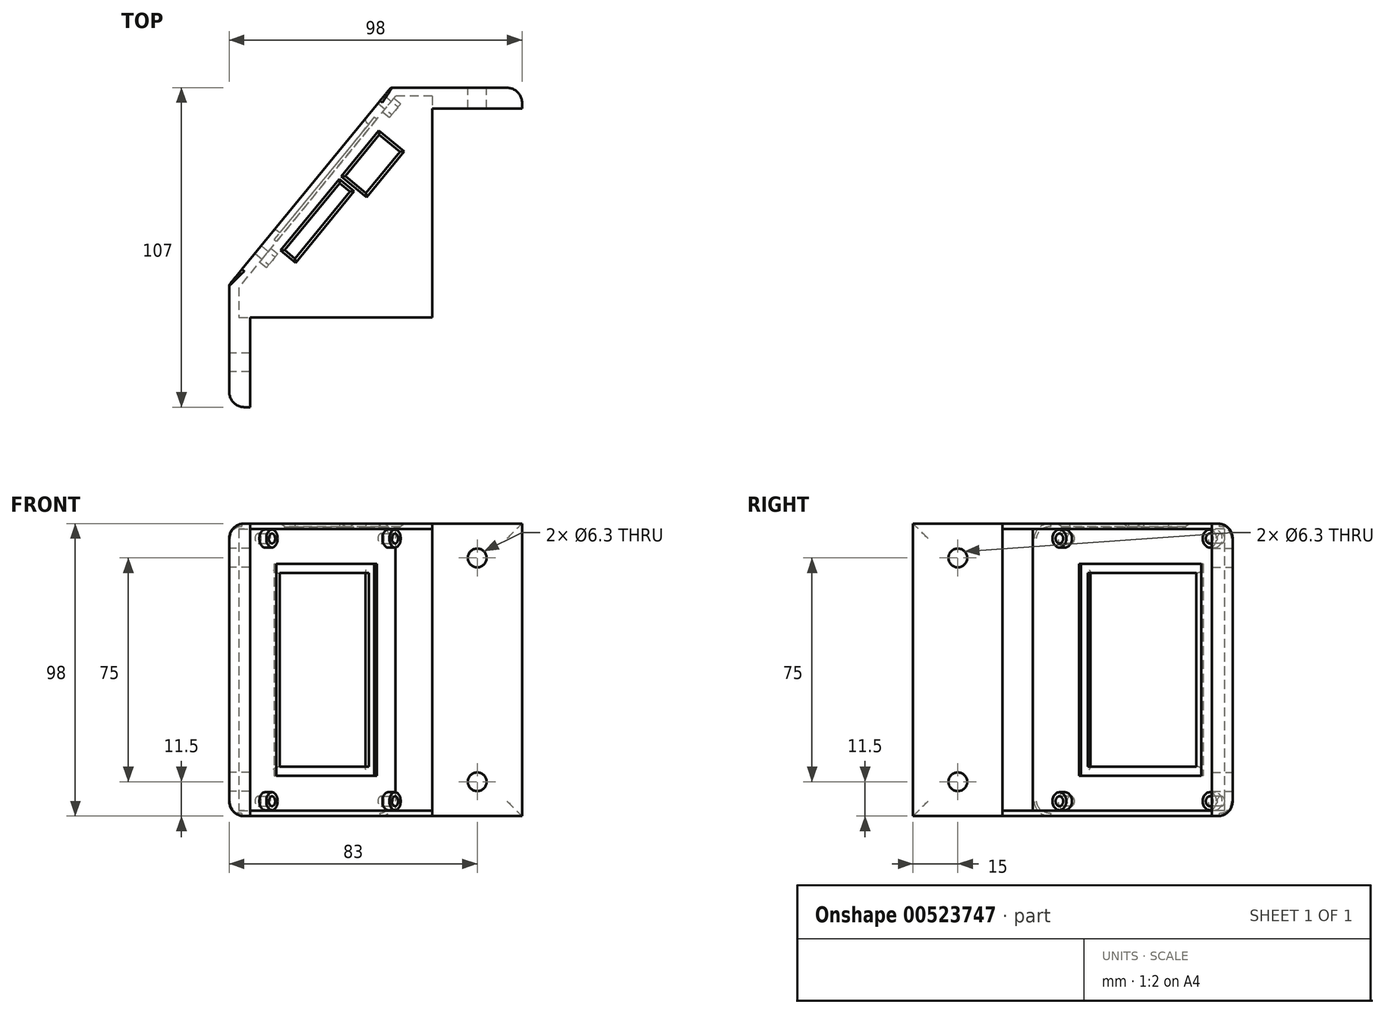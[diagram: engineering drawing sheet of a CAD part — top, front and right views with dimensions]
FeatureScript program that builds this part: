
annotation { "Feature Type Name" : "Feature", "Feature Type Description" : "" }
export const myFeature = defineFeature(function(context is Context, id is Id, definition is map)
    precondition{}
    {
        {
            var Q0;
            Q0=qCreatedBy(makeId("Top.planeOp"),FACE);
            var sketch = newSketch(context, id + "F0", { "sketchPlane" : qUnion([Q0])});
            skLineSegment(sketch, "E0.bottom", {"start": v(0, 0) * mm, "end": v(30, 0) * mm, "construction": true});
            skLineSegment(sketch, "E0.top", {"start": v(0, 30) * mm, "end": v(30, 30) * mm, "construction": true});
            skLineSegment(sketch, "E0.left", {"start": v(0, 0) * mm, "end": v(0, 30) * mm, "construction": true});
            skLineSegment(sketch, "E0.right", {"start": v(30, 0) * mm, "end": v(30, 30) * mm, "construction": true});
            skLineSegment(sketch, "E1.bottom", {"start": v(61, 70) * mm, "end": v(91, 70) * mm, "construction": true});
            skLineSegment(sketch, "E1.top", {"start": v(61, 100) * mm, "end": v(91, 100) * mm, "construction": true});
            skLineSegment(sketch, "E1.left", {"start": v(61, 70) * mm, "end": v(61, 100) * mm, "construction": true});
            skLineSegment(sketch, "E1.right", {"start": v(91, 70) * mm, "end": v(91, 100) * mm, "construction": true});
            skLineSegment(sketch, "E2", {"start": v(61, 70) * mm, "end": v(61, 100) * mm});
            skLineSegment(sketch, "E3", {"start": v(60.77, 119.05) * mm, "end": v(-24.85, 14.49) * mm});
            skLineSegment(sketch, "E4", {"start": v(61, 94.07) * mm, "end": v(8.54, 30) * mm, "construction": true});
            skLineSegment(sketch, "E5", {"start": v(61, 94.07) * mm, "end": v(48.62, 104.2) * mm, "construction": true});
            skLineSegment(sketch, "E6", {"start": v(8.54, 30) * mm, "end": v(-3.84, 40.14) * mm, "construction": true});
            skLineSegment(sketch, "E7", {"start": v(-4.85, 0) * mm, "end": v(0, 0) * mm});
            skLineSegment(sketch, "E8", {"start": v(51.37, 112.3) * mm, "end": v(-39.42, 1.43) * mm});
            skLineSegment(sketch, "E9", {"start": v(91, 100) * mm, "end": v(91, 107) * mm});
            skLineSegment(sketch, "E10", {"start": v(91, 107) * mm, "end": v(47.03, 107) * mm});
            skLineSegment(sketch, "E11", {"start": v(0, 0) * mm, "end": v(-7, 0) * mm});
            skLineSegment(sketch, "E12", {"start": v(-7, 0) * mm, "end": v(-7, 41.02) * mm});
            skLineSegment(sketch, "E13", {"start": v(91, 100) * mm, "end": v(61, 100) * mm});
            skLineSegment(sketch, "E14", {"start": v(61, 104.2) * mm, "end": v(61, 100) * mm});
            skLineSegment(sketch, "E15", {"start": v(61, 104.2) * mm, "end": v(48.62, 104.2) * mm});
            skLineSegment(sketch, "E16", {"start": v(-3.84, 40.14) * mm, "end": v(-3.84, 30) * mm});
            skLineSegment(sketch, "E17", {"start": v(-3.84, 30) * mm, "end": v(0, 30) * mm});
            skLineSegment(sketch, "E18", {"start": v(0, 30) * mm, "end": v(0, 0) * mm});
            skSolve(sketch);
        }
        {
            var Q0;
            Q0 = qSketchRegion(id + "F0", true);
            extrude(context, id + "F1", {"entities" : qUnion([Q0]), "depth" : 98 * mm, "offsetDistance" : 25 * mm});
        }
        {
            var Q0;
            Q0=makeQuery(id+"F1.opExtrude","SWEPT_FACE",FACE,{"disambiguationData":[OSD([sQuery(id+"F0.wireOp",EDGE,"E3")])]});
            var sketch = newSketch(context, id + "F2", { "sketchPlane" : qUnion([Q0])});
            skLineSegment(sketch, "E19", {"start": v(70.02, 98) * mm, "end": v(70.02, 0) * mm, "construction": true});
            skLineSegment(sketch, "E20", {"start": v(111.43, 49) * mm, "end": v(28.62, 49) * mm, "construction": true});
            skLineSegment(sketch, "E21.bottom", {"start": v(98.52, 81.5) * mm, "end": v(51.52, 81.5) * mm});
            skLineSegment(sketch, "E21.top", {"start": v(98.52, 16.5) * mm, "end": v(51.52, 16.5) * mm});
            skLineSegment(sketch, "E21.left", {"start": v(98.52, 81.5) * mm, "end": v(98.52, 16.5) * mm});
            skLineSegment(sketch, "E21.right", {"start": v(51.52, 81.5) * mm, "end": v(51.52, 16.5) * mm});
            skLineSegment(sketch, "E22.0", {"start": v(48.52, 84.5) * mm, "end": v(48.52, 13.5) * mm});
            skLineSegment(sketch, "E22.1", {"start": v(101.52, 84.5) * mm, "end": v(48.52, 84.5) * mm});
            skLineSegment(sketch, "E22.2", {"start": v(101.52, 84.5) * mm, "end": v(101.52, 13.5) * mm});
            skLineSegment(sketch, "E22.3", {"start": v(101.52, 13.5) * mm, "end": v(48.52, 13.5) * mm});
            skSolve(sketch);
        }
        {
            var Q0;
            Q0=makeQuery(id+"F2.imprint","IMPRINT",FACE,{"disambiguationData":[TD([[makeQuery(id+"F2.imprint","IMPRINT",EDGE,{"derivedFrom":sQuery(id+"F2.wireOp",EDGE,"E21.bottom")}),1.0]])]});
            extrude(context, id + "F3", {"entities" : qUnion([Q0]), "operationType" : NewBodyOperationType.REMOVE, "oppositeDirection" : true, "depth" : 25 * mm, "offsetDistance" : 25 * mm});
        }
        {
            var Q0;
            Q0=makeQuery(id+"F2.imprint","IMPRINT",FACE,{"disambiguationData":[TD([[makeQuery(id+"F2.imprint","IMPRINT",EDGE,{"derivedFrom":sQuery(id+"F2.wireOp",EDGE,"E21.bottom")}),-1.0]])]});
            extrude(context, id + "F4", {"entities" : qUnion([Q0]), "operationType" : NewBodyOperationType.REMOVE, "oppositeDirection" : true, "depth" : 1 * mm, "offsetDistance" : 25 * mm});
        }
        {
            var Q0;
            Q0=makeQuery(id+"F2.imprint","IMPRINT",FACE,{"disambiguationData":[TD([[makeQuery(id+"F2.imprint","IMPRINT",EDGE,{"derivedFrom":sQuery(id+"F2.wireOp",EDGE,"E21.bottom")}),-1.0]])]});
            var sketch = newSketch(context, id + "F5", { "sketchPlane" : qUnion([Q0])});
            skLineSegment(sketch, "E23", {"start": v(75.02, 88.6) * mm, "end": v(75.02, 4.4) * mm, "construction": true});
            skCircle(sketch, "E24", {"center": v(107.52, 5) * mm, "radius": 1.65 * mm});
            skCircle(sketch, "E25", {"center": v(42.52, 5) * mm, "radius": 1.65 * mm});
            skCircle(sketch, "E26.MirrorC", {"center": v(107.52, 93) * mm, "radius": 1.65 * mm});
            skCircle(sketch, "E27.MirrorC", {"center": v(42.52, 93) * mm, "radius": 1.65 * mm});
            skSolve(sketch);
        }
        {
            var Q0;
            Q0 = qSketchRegion(id + "F5", true);
            extrude(context, id + "F6", {"entities" : qUnion([Q0]), "operationType" : NewBodyOperationType.REMOVE, "oppositeDirection" : true, "depth" : 25 * mm, "offsetDistance" : 25 * mm});
        }
        {
            var Q0;
            Q0=makeQuery(id+"F2.imprint","IMPRINT",FACE,{"disambiguationData":[TD([[makeQuery(id+"F2.imprint","IMPRINT",EDGE,{"derivedFrom":sQuery(id+"F2.wireOp",EDGE,"E22.0")}),-1.0]])]});
            var sketch = newSketch(context, id + "F7", { "sketchPlane" : qUnion([Q0])});
            skCircle(sketch, "E28", {"center": v(107.52, 93) * mm, "radius": 3 * mm});
            skCircle(sketch, "E29", {"center": v(42.52, 93) * mm, "radius": 3 * mm});
            skCircle(sketch, "E30", {"center": v(107.52, 93) * mm, "radius": 1.65 * mm});
            skCircle(sketch, "E31", {"center": v(42.52, 93) * mm, "radius": 1.65 * mm});
            skCircle(sketch, "E32.MirrorC", {"center": v(107.52, 5) * mm, "radius": 1.65 * mm});
            skCircle(sketch, "E33.MirrorC", {"center": v(42.52, 5) * mm, "radius": 1.65 * mm});
            skCircle(sketch, "E34.MirrorC", {"center": v(107.52, 5) * mm, "radius": 3 * mm});
            skCircle(sketch, "E35.MirrorC", {"center": v(42.52, 5) * mm, "radius": 3 * mm});
            skSolve(sketch);
        }
        {
            var Q0;
            Q0 = qSketchRegion(id + "F7", true);
            extrude(context, id + "F8", {"entities" : qUnion([Q0]), "operationType" : NewBodyOperationType.ADD, "depth" : 3 * mm, "offsetDistance" : 25 * mm});
        }
        {
            var Q0;
            Q0=makeQuery(id+"F3.boolean.opBoolean","INTERSECT",EDGE,{"derivedFrom":[makeQuery(id+"F1.opExtrude","SWEPT_FACE",FACE,{"disambiguationData":[OSD([sQuery(id+"F0.wireOp",EDGE,"E8")])]}),makeQuery(id+"F3.opExtrude","SWEPT_FACE",FACE,{"disambiguationData":[OSD([sQuery(id+"F2.wireOp",EDGE,"E21.left")])]})]});
            var Q1;
            Q1=makeQuery(id+"F3.boolean.opBoolean","INTERSECT",EDGE,{"derivedFrom":[makeQuery(id+"F1.opExtrude","SWEPT_FACE",FACE,{"disambiguationData":[OSD([sQuery(id+"F0.wireOp",EDGE,"E8")])]}),makeQuery(id+"F3.opExtrude","SWEPT_FACE",FACE,{"disambiguationData":[OSD([sQuery(id+"F2.wireOp",EDGE,"E21.bottom")])]})]});
            var Q2;
            Q2=makeQuery(id+"F3.boolean.opBoolean","INTERSECT",EDGE,{"derivedFrom":[makeQuery(id+"F1.opExtrude","SWEPT_FACE",FACE,{"disambiguationData":[OSD([sQuery(id+"F0.wireOp",EDGE,"E8")])]}),makeQuery(id+"F3.opExtrude","SWEPT_FACE",FACE,{"disambiguationData":[OSD([sQuery(id+"F2.wireOp",EDGE,"E21.right")])]})]});
            var Q3;
            Q3=makeQuery(id+"F3.boolean.opBoolean","INTERSECT",EDGE,{"derivedFrom":[makeQuery(id+"F1.opExtrude","SWEPT_FACE",FACE,{"disambiguationData":[OSD([sQuery(id+"F0.wireOp",EDGE,"E8")])]}),makeQuery(id+"F3.opExtrude","SWEPT_FACE",FACE,{"disambiguationData":[OSD([sQuery(id+"F2.wireOp",EDGE,"E21.top")])]})]});
            fillet(context, id + "F9", {"entities" : qUnion([Q0, Q1, Q2, Q3]), "radius" : 1 * mm, "tangentPropagation" : true, "allowEdgeOverflow" : false});
        }
        {
            var Q0;
            Q0=makeQuery(id+"F1.opExtrude","SWEPT_FACE",FACE,{"disambiguationData":[OSD([sQuery(id+"F0.wireOp",EDGE,"E10")])]});
            var sketch = newSketch(context, id + "F10", { "sketchPlane" : qUnion([Q0])});
            skCircle(sketch, "E36", {"center": v(-76, 86.5) * mm, "radius": 3.15 * mm});
            skCircle(sketch, "E37", {"center": v(-76, 11.5) * mm, "radius": 3.15 * mm});
            skSolve(sketch);
        }
        {
            var Q0;
            Q0 = qSketchRegion(id + "F10", true);
            extrude(context, id + "F11", {"entities" : qUnion([Q0]), "operationType" : NewBodyOperationType.REMOVE, "oppositeDirection" : true, "depth" : 25 * mm, "offsetDistance" : 25 * mm});
        }
        {
            var Q0;
            Q0=makeQuery(id+"F1.opExtrude","SWEPT_FACE",FACE,{"disambiguationData":[OSD([sQuery(id+"F0.wireOp",EDGE,"E12")])]});
            var sketch = newSketch(context, id + "F12", { "sketchPlane" : qUnion([Q0])});
            skCircle(sketch, "E38", {"center": v(-15, 86.5) * mm, "radius": 3.15 * mm});
            skCircle(sketch, "E39", {"center": v(-15, 11.5) * mm, "radius": 3.15 * mm});
            skSolve(sketch);
        }
        {
            var Q0;
            Q0 = qSketchRegion(id + "F12", true);
            extrude(context, id + "F13", {"entities" : qUnion([Q0]), "operationType" : NewBodyOperationType.REMOVE, "oppositeDirection" : true, "depth" : 25 * mm, "offsetDistance" : 25 * mm});
        }
        {
            var Q0;
            Q0=makeQuery(id+"F1.opExtrude","CAP_FACE",FACE,{"disambiguationData":[OSD([sQuery(id+"F0.wireOp",EDGE,"E3"),sQuery(id+"F0.wireOp",EDGE,"E8"),sQuery(id+"F0.wireOp",EDGE,"E9"),sQuery(id+"F0.wireOp",EDGE,"E10"),sQuery(id+"F0.wireOp",EDGE,"E11"),sQuery(id+"F0.wireOp",EDGE,"E12"),sQuery(id+"F0.wireOp",EDGE,"E13"),sQuery(id+"F0.wireOp",EDGE,"E14"),sQuery(id+"F0.wireOp",EDGE,"E15"),sQuery(id+"F0.wireOp",EDGE,"E16"),sQuery(id+"F0.wireOp",EDGE,"E17"),sQuery(id+"F0.wireOp",EDGE,"E18")])],"isStart":true});
            var sketch = newSketch(context, id + "F14", { "sketchPlane" : qUnion([Q0])});
            skLineSegment(sketch, "E40.bottom", {"start": v(0, 0) * mm, "end": v(30, 0) * mm, "construction": true});
            skLineSegment(sketch, "E40.top", {"start": v(0, -30) * mm, "end": v(30, -30) * mm, "construction": true});
            skLineSegment(sketch, "E40.left", {"start": v(0, 0) * mm, "end": v(0, -30) * mm, "construction": true});
            skLineSegment(sketch, "E40.right", {"start": v(30, 0) * mm, "end": v(30, -30) * mm, "construction": true});
            skLineSegment(sketch, "E41.bottom", {"start": v(61, -100) * mm, "end": v(91, -100) * mm, "construction": true});
            skLineSegment(sketch, "E41.top", {"start": v(61, -70) * mm, "end": v(91, -70) * mm, "construction": true});
            skLineSegment(sketch, "E41.left", {"start": v(61, -100) * mm, "end": v(61, -70) * mm, "construction": true});
            skLineSegment(sketch, "E41.right", {"start": v(91, -100) * mm, "end": v(91, -70) * mm, "construction": true});
            skLineSegment(sketch, "E42", {"start": v(-3.84, -30) * mm, "end": v(61, -30) * mm});
            skLineSegment(sketch, "E43", {"start": v(61, -30) * mm, "end": v(61, -104.2) * mm});
            skLineSegment(sketch, "E44", {"start": v(61, -104.2) * mm, "end": v(48.62, -104.2) * mm});
            skLineSegment(sketch, "E45", {"start": v(48.62, -104.2) * mm, "end": v(-3.84, -40.14) * mm});
            skLineSegment(sketch, "E46", {"start": v(-3.84, -40.14) * mm, "end": v(-3.84, -30) * mm});
            skSolve(sketch);
        }
        {
            var Q0;
            Q0 = qSketchRegion(id + "F14", true);
            extrude(context, id + "F15", {"entities" : qUnion([Q0]), "operationType" : NewBodyOperationType.ADD, "oppositeDirection" : true, "depth" : 1.8 * mm, "offsetDistance" : 25 * mm});
        }
        {
            var Q0;
            Q0=makeQuery(id+"F1.opExtrude","CAP_FACE",FACE,{"disambiguationData":[OSD([sQuery(id+"F0.wireOp",EDGE,"E3"),sQuery(id+"F0.wireOp",EDGE,"E8"),sQuery(id+"F0.wireOp",EDGE,"E9"),sQuery(id+"F0.wireOp",EDGE,"E10"),sQuery(id+"F0.wireOp",EDGE,"E11"),sQuery(id+"F0.wireOp",EDGE,"E12"),sQuery(id+"F0.wireOp",EDGE,"E13"),sQuery(id+"F0.wireOp",EDGE,"E14"),sQuery(id+"F0.wireOp",EDGE,"E15"),sQuery(id+"F0.wireOp",EDGE,"E16"),sQuery(id+"F0.wireOp",EDGE,"E17"),sQuery(id+"F0.wireOp",EDGE,"E18")])],"isStart":false});
            var sketch = newSketch(context, id + "F16", { "sketchPlane" : qUnion([Q0])});
            skLineSegment(sketch, "E47", {"start": v(61, 104.2) * mm, "end": v(61, 30) * mm});
            skLineSegment(sketch, "E48", {"start": v(61, 30) * mm, "end": v(-3.84, 30) * mm});
            skLineSegment(sketch, "E49", {"start": v(-3.84, 30) * mm, "end": v(-3.84, 40.14) * mm});
            skLineSegment(sketch, "E50", {"start": v(-3.84, 40.14) * mm, "end": v(48.62, 104.2) * mm});
            skLineSegment(sketch, "E51", {"start": v(48.62, 104.2) * mm, "end": v(61, 104.2) * mm});
            skLineSegment(sketch, "E52", {"start": v(43.22, 91.3) * mm, "end": v(46.32, 88.77) * mm});
            skLineSegment(sketch, "E53", {"start": v(31.82, 77.38) * mm, "end": v(34.55, 75.14) * mm});
            skLineSegment(sketch, "E54", {"start": v(29.92, 75.05) * mm, "end": v(33.4, 72.2) * mm});
            skLineSegment(sketch, "E55", {"start": v(11.55, 52.62) * mm, "end": v(14.98, 49.8) * mm});
            skLineSegment(sketch, "E56", {"start": v(43.22, 91.3) * mm, "end": v(31.82, 77.38) * mm});
            skLineSegment(sketch, "E57", {"start": v(50.19, 85.6) * mm, "end": v(38.78, 71.67) * mm});
            skLineSegment(sketch, "E58", {"start": v(46.32, 88.77) * mm, "end": v(50.19, 85.6) * mm});
            skLineSegment(sketch, "E59", {"start": v(34.55, 75.14) * mm, "end": v(38.78, 71.67) * mm});
            skLineSegment(sketch, "E60", {"start": v(33.4, 72.2) * mm, "end": v(15.03, 49.77) * mm});
            skLineSegment(sketch, "E61.trimOffspring", {"start": v(29.92, 75.05) * mm, "end": v(11.55, 52.62) * mm});
            skPoint(sketch, "E62.orphan", {"position": v(40.13, 93.84) * mm});
            skPoint(sketch, "E63.orphan", {"position": v(8.45, 55.15) * mm});
            skLineSegment(sketch, "E64", {"start": v(15.03, 49.77) * mm, "end": v(14.98, 49.8) * mm});
            skSolve(sketch);
        }
        {
            var Q0;
            Q0 = qSketchRegion(id + "F16", true);
            extrude(context, id + "F17", {"entities" : qUnion([Q0]), "operationType" : NewBodyOperationType.ADD, "oppositeDirection" : true, "depth" : 1.8 * mm, "offsetDistance" : 25 * mm});
        }
        {
            var Q0;
            Q0=makeQuery(id+"F1.opExtrude","SWEPT_EDGE",EDGE,{"disambiguationData":[OSD([sQuery(id+"F0.wireOp",EDGE,"E9"),sQuery(id+"F0.wireOp",EDGE,"E10")])]});
            var Q1;
            Q1=makeQuery(id+"F1.opExtrude","CAP_EDGE",EDGE,{"disambiguationData":[OSD([sQuery(id+"F0.wireOp",EDGE,"E10")])],"isStart":true});
            var Q2;
            Q2=makeQuery(id+"F1.opExtrude","CAP_EDGE",EDGE,{"disambiguationData":[OSD([sQuery(id+"F0.wireOp",EDGE,"E10")])],"isStart":false});
            var Q3;
            Q3=makeQuery(id+"F1.opExtrude","CAP_EDGE",EDGE,{"disambiguationData":[OSD([sQuery(id+"F0.wireOp",EDGE,"E12")])],"isStart":false});
            var Q4;
            Q4=makeQuery(id+"F1.opExtrude","SWEPT_EDGE",EDGE,{"disambiguationData":[OSD([sQuery(id+"F0.wireOp",EDGE,"E11"),sQuery(id+"F0.wireOp",EDGE,"E12")])]});
            var Q5;
            Q5=makeQuery(id+"F1.opExtrude","CAP_EDGE",EDGE,{"disambiguationData":[OSD([sQuery(id+"F0.wireOp",EDGE,"E12")])],"isStart":true});
            fillet(context, id + "F18", {"entities" : qUnion([Q0, Q1, Q2, Q3, Q4, Q5]), "radius" : 5 * mm, "tangentPropagation" : true, "allowEdgeOverflow" : false});
        }
        {
            var Q0;
            Q0=makeQuery(id+"F1.opExtrude","CAP_EDGE",EDGE,{"disambiguationData":[OSD([sQuery(id+"F0.wireOp",EDGE,"E8")])],"isStart":false});
            fillet(context, id + "F19", {"entities" : qUnion([Q0]), "radius" : 1 * mm, "tangentPropagation" : true, "allowEdgeOverflow" : false});
        }
        {
            var Q0;
            Q0=makeQuery(id+"F17.opExtrude","CAP_EDGE",EDGE,{"disambiguationData":[OSD([sQuery(id+"F16.wireOp",EDGE,"E57")])],"isStart":true});
            var Q1;
            Q1=makeQuery(id+"F17.opExtrude","CAP_EDGE",EDGE,{"disambiguationData":[OSD([sQuery(id+"F16.wireOp",EDGE,"E52"),sQuery(id+"F16.wireOp",EDGE,"E58")])],"isStart":true});
            var Q2;
            Q2=makeQuery(id+"F17.opExtrude","CAP_EDGE",EDGE,{"disambiguationData":[OSD([sQuery(id+"F16.wireOp",EDGE,"E56")])],"isStart":true});
            var Q3;
            Q3=makeQuery(id+"F17.opExtrude","CAP_EDGE",EDGE,{"disambiguationData":[OSD([sQuery(id+"F16.wireOp",EDGE,"E53"),sQuery(id+"F16.wireOp",EDGE,"E59")])],"isStart":true});
            var Q4;
            Q4=makeQuery(id+"F17.opExtrude","CAP_EDGE",EDGE,{"disambiguationData":[OSD([sQuery(id+"F16.wireOp",EDGE,"E54")])],"isStart":true});
            var Q5;
            Q5=makeQuery(id+"F17.opExtrude","CAP_EDGE",EDGE,{"disambiguationData":[OSD([sQuery(id+"F16.wireOp",EDGE,"E60")])],"isStart":true});
            var Q6;
            Q6=makeQuery(id+"F17.opExtrude","CAP_EDGE",EDGE,{"disambiguationData":[OSD([sQuery(id+"F16.wireOp",EDGE,"E61.trimOffspring")])],"isStart":true});
            var Q7;
            Q7=makeQuery(id+"F17.opExtrude","CAP_EDGE",EDGE,{"disambiguationData":[OSD([sQuery(id+"F16.wireOp",EDGE,"E55"),sQuery(id+"F16.wireOp",EDGE,"E64")])],"isStart":true});
            chamfer(context, id + "F20", {"entities" : qUnion([Q0, Q1, Q2, Q3, Q4, Q5, Q6, Q7]), "width" : 1 * mm, "tangentPropagation" : true});
        }
    });
